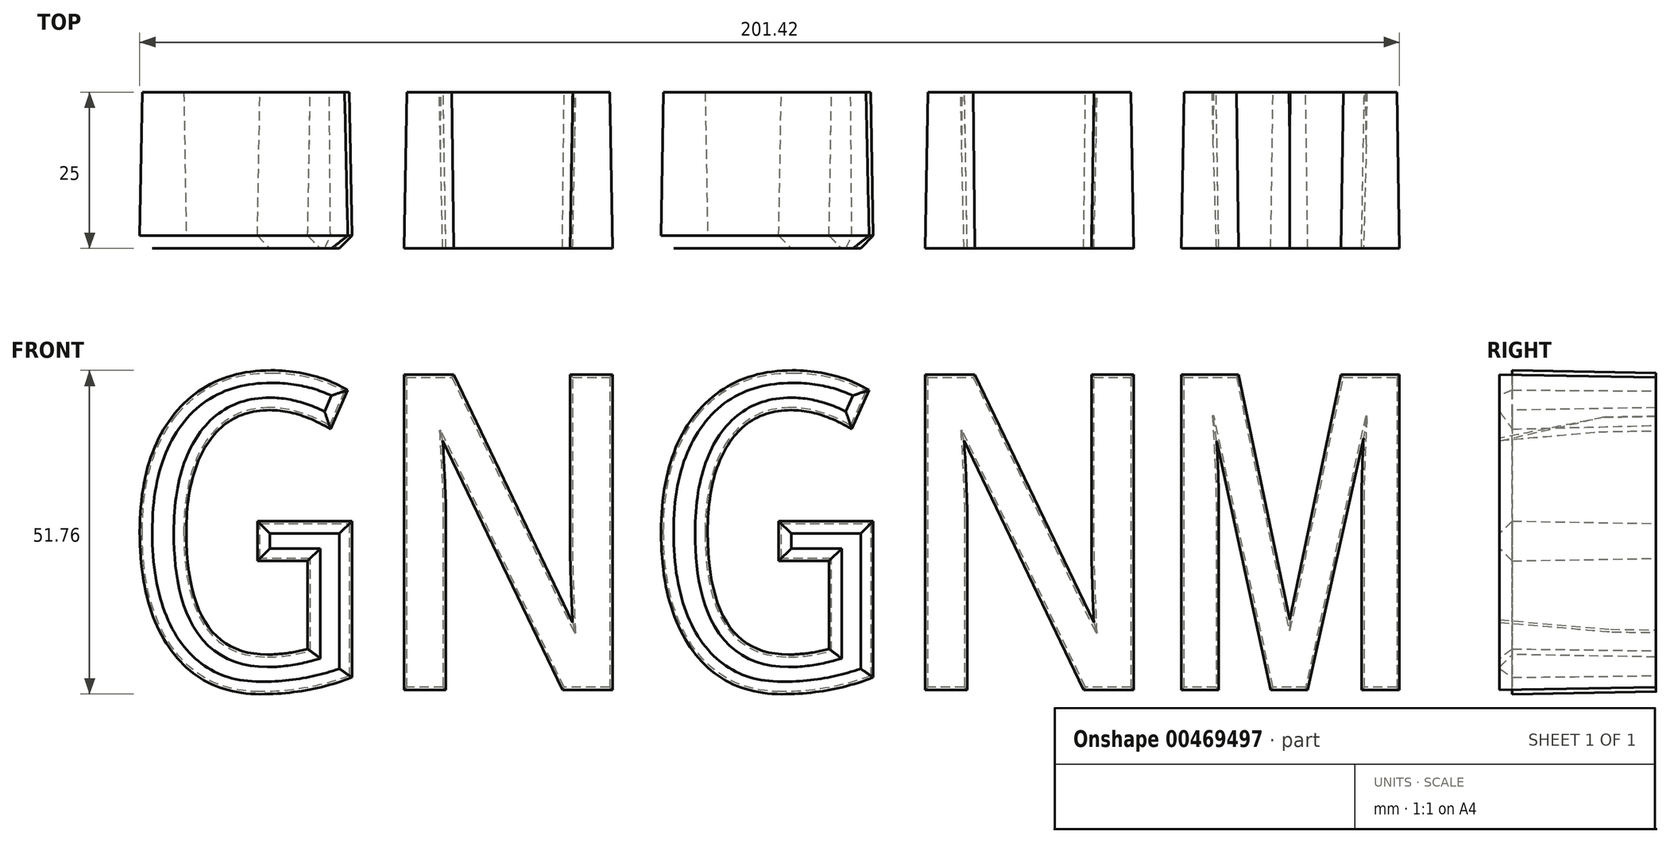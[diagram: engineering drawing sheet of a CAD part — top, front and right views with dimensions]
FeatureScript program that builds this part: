
annotation { "Feature Type Name" : "Feature", "Feature Type Description" : "" }
export const myFeature = defineFeature(function(context is Context, id is Id, definition is map)
    precondition{}
    {
        {
            var Q0;
            Q0=qCreatedBy(makeId("Front.planeOp"),FACE);
            var sketch = newSketch(context, id + "F0", { "sketchPlane" : qUnion([Q0])});
            skText(sketch, "E0", { "text": "GNGNM", "fontName": "DroidSansMono.ttf"});
            const initialGuessF0  = {"E0": [-0.03023, -0.02295, 1, 0, 0.05]};
            skSetInitialGuess(sketch, initialGuessF0);
            skSolve(sketch);
        }
        {
            var Q0;
            Q0=makeQuery(id+"F0.imprint","IMPRINT",FACE,{"disambiguationData":[TD([[makeQuery(id+"F0.imprint","IMPRINT",EDGE,{"derivedFrom":sQuery(id+"F0.wireOp",EDGE,"E0.sketch_text.stroke-17")}),-1.0]])]});
            var Q1;
            Q1=makeQuery(id+"F0.imprint","IMPRINT",FACE,{"disambiguationData":[TD([[makeQuery(id+"F0.imprint","IMPRINT",EDGE,{"derivedFrom":sQuery(id+"F0.wireOp",EDGE,"E0.sketch_text.stroke-0")}),-1.0]])]});
            var Q2;
            Q2=makeQuery(id+"F0.imprint","IMPRINT",FACE,{"disambiguationData":[TD([[makeQuery(id+"F0.imprint","IMPRINT",EDGE,{"derivedFrom":sQuery(id+"F0.wireOp",EDGE,"E0.sketch_text.stroke-31")}),-1.0]])]});
            var Q3;
            Q3=makeQuery(id+"F0.imprint","IMPRINT",FACE,{"disambiguationData":[TD([[makeQuery(id+"F0.imprint","IMPRINT",EDGE,{"derivedFrom":sQuery(id+"F0.wireOp",EDGE,"E0.sketch_text.stroke-48")}),-1.0]])]});
            var Q4;
            Q4=makeQuery(id+"F0.imprint","IMPRINT",FACE,{"disambiguationData":[TD([[makeQuery(id+"F0.imprint","IMPRINT",EDGE,{"derivedFrom":sQuery(id+"F0.wireOp",EDGE,"E0.sketch_text.stroke-62")}),-1.0]])]});
            extrude(context, id + "F1", {"entities" : qUnion([Q0, Q1, Q2, Q3, Q4]), "depth" : 25 * mm, "hasDraft" : true, "draftAngle" : 1 * degree});
        }
        {
            var Q0;
            Q0=makeQuery(id+"F1.opExtrude","CAP_EDGE",EDGE,{"disambiguationData":[OSD([sQuery(id+"F0.wireOp",EDGE,"E0.sketch_text.stroke-9")])],"isStart":false});
            var Q1;
            Q1=makeQuery(id+"F1.opExtrude","CAP_EDGE",EDGE,{"disambiguationData":[OSD([sQuery(id+"F0.wireOp",EDGE,"E0.sketch_text.stroke-10")])],"isStart":false});
            var Q2;
            Q2=makeQuery(id+"F1.opExtrude","CAP_EDGE",EDGE,{"disambiguationData":[OSD([sQuery(id+"F0.wireOp",EDGE,"E0.sketch_text.stroke-11")])],"isStart":false});
            var Q3;
            Q3=makeQuery(id+"F1.opExtrude","CAP_EDGE",EDGE,{"disambiguationData":[OSD([sQuery(id+"F0.wireOp",EDGE,"E0.sketch_text.stroke-12")])],"isStart":false});
            var Q4;
            Q4=makeQuery(id+"F1.opExtrude","CAP_EDGE",EDGE,{"disambiguationData":[OSD([sQuery(id+"F0.wireOp",EDGE,"E0.sketch_text.stroke-13")])],"isStart":false});
            var Q5;
            Q5=makeQuery(id+"F1.opExtrude","CAP_EDGE",EDGE,{"disambiguationData":[OSD([sQuery(id+"F0.wireOp",EDGE,"E0.sketch_text.stroke-14")])],"isStart":false});
            var Q6;
            Q6=makeQuery(id+"F1.opExtrude","CAP_EDGE",EDGE,{"disambiguationData":[OSD([sQuery(id+"F0.wireOp",EDGE,"E0.sketch_text.stroke-15")])],"isStart":false});
            var Q7;
            Q7=makeQuery(id+"F1.opExtrude","CAP_EDGE",EDGE,{"disambiguationData":[OSD([sQuery(id+"F0.wireOp",EDGE,"E0.sketch_text.stroke-16")])],"isStart":false});
            var Q8;
            Q8=makeQuery(id+"F1.opExtrude","CAP_EDGE",EDGE,{"disambiguationData":[OSD([sQuery(id+"F0.wireOp",EDGE,"E0.sketch_text.stroke-0")])],"isStart":false});
            var Q9;
            Q9=makeQuery(id+"F1.opExtrude","CAP_EDGE",EDGE,{"disambiguationData":[OSD([sQuery(id+"F0.wireOp",EDGE,"E0.sketch_text.stroke-1")])],"isStart":false});
            var Q10;
            Q10=makeQuery(id+"F1.opExtrude","CAP_EDGE",EDGE,{"disambiguationData":[OSD([sQuery(id+"F0.wireOp",EDGE,"E0.sketch_text.stroke-2")])],"isStart":false});
            var Q11;
            Q11=makeQuery(id+"F1.opExtrude","CAP_EDGE",EDGE,{"disambiguationData":[OSD([sQuery(id+"F0.wireOp",EDGE,"E0.sketch_text.stroke-3")])],"isStart":false});
            var Q12;
            Q12=makeQuery(id+"F1.opExtrude","CAP_EDGE",EDGE,{"disambiguationData":[OSD([sQuery(id+"F0.wireOp",EDGE,"E0.sketch_text.stroke-4")])],"isStart":false});
            var Q13;
            Q13=makeQuery(id+"F1.opExtrude","CAP_EDGE",EDGE,{"disambiguationData":[OSD([sQuery(id+"F0.wireOp",EDGE,"E0.sketch_text.stroke-5")])],"isStart":false});
            var Q14;
            Q14=makeQuery(id+"F1.opExtrude","CAP_EDGE",EDGE,{"disambiguationData":[OSD([sQuery(id+"F0.wireOp",EDGE,"E0.sketch_text.stroke-6")])],"isStart":false});
            var Q15;
            Q15=makeQuery(id+"F1.opExtrude","CAP_EDGE",EDGE,{"disambiguationData":[OSD([sQuery(id+"F0.wireOp",EDGE,"E0.sketch_text.stroke-7")])],"isStart":false});
            var Q16;
            Q16=makeQuery(id+"F1.opExtrude","CAP_EDGE",EDGE,{"disambiguationData":[OSD([sQuery(id+"F0.wireOp",EDGE,"E0.sketch_text.stroke-8")])],"isStart":false});
            var Q17;
            Q17=makeQuery(id+"F1.opExtrude","CAP_EDGE",EDGE,{"disambiguationData":[OSD([sQuery(id+"F0.wireOp",EDGE,"E0.sketch_text.stroke-23")])],"isStart":false});
            var Q18;
            Q18=makeQuery(id+"F1.opExtrude","CAP_EDGE",EDGE,{"disambiguationData":[OSD([sQuery(id+"F0.wireOp",EDGE,"E0.sketch_text.stroke-22")])],"isStart":false});
            var Q19;
            Q19=makeQuery(id+"F1.opExtrude","CAP_EDGE",EDGE,{"disambiguationData":[OSD([sQuery(id+"F0.wireOp",EDGE,"E0.sketch_text.stroke-21")])],"isStart":false});
            var Q20;
            Q20=makeQuery(id+"F1.opExtrude","CAP_EDGE",EDGE,{"disambiguationData":[OSD([sQuery(id+"F0.wireOp",EDGE,"E0.sketch_text.stroke-20")])],"isStart":false});
            var Q21;
            Q21=makeQuery(id+"F1.opExtrude","CAP_EDGE",EDGE,{"disambiguationData":[OSD([sQuery(id+"F0.wireOp",EDGE,"E0.sketch_text.stroke-18")])],"isStart":false});
            var Q22;
            Q22=makeQuery(id+"F1.opExtrude","CAP_EDGE",EDGE,{"disambiguationData":[OSD([sQuery(id+"F0.wireOp",EDGE,"E0.sketch_text.stroke-24")])],"isStart":false});
            var Q23;
            Q23=makeQuery(id+"F1.opExtrude","CAP_EDGE",EDGE,{"disambiguationData":[OSD([sQuery(id+"F0.wireOp",EDGE,"E0.sketch_text.stroke-25")])],"isStart":false});
            var Q24;
            Q24=makeQuery(id+"F1.opExtrude","CAP_EDGE",EDGE,{"disambiguationData":[OSD([sQuery(id+"F0.wireOp",EDGE,"E0.sketch_text.stroke-28")])],"isStart":false});
            var Q25;
            Q25=makeQuery(id+"F1.opExtrude","CAP_EDGE",EDGE,{"disambiguationData":[OSD([sQuery(id+"F0.wireOp",EDGE,"E0.sketch_text.stroke-29")])],"isStart":false});
            var Q26;
            Q26=makeQuery(id+"F1.opExtrude","CAP_EDGE",EDGE,{"disambiguationData":[OSD([sQuery(id+"F0.wireOp",EDGE,"E0.sketch_text.stroke-30")])],"isStart":false});
            var Q27;
            Q27=makeQuery(id+"F1.opExtrude","CAP_EDGE",EDGE,{"disambiguationData":[OSD([sQuery(id+"F0.wireOp",EDGE,"E0.sketch_text.stroke-17")])],"isStart":false});
            var Q28;
            Q28=makeQuery(id+"F1.opExtrude","CAP_EDGE",EDGE,{"disambiguationData":[OSD([sQuery(id+"F0.wireOp",EDGE,"E0.sketch_text.stroke-33")])],"isStart":false});
            var Q29;
            Q29=makeQuery(id+"F1.opExtrude","CAP_EDGE",EDGE,{"disambiguationData":[OSD([sQuery(id+"F0.wireOp",EDGE,"E0.sketch_text.stroke-34")])],"isStart":false});
            var Q30;
            Q30=makeQuery(id+"F1.opExtrude","CAP_EDGE",EDGE,{"disambiguationData":[OSD([sQuery(id+"F0.wireOp",EDGE,"E0.sketch_text.stroke-35")])],"isStart":false});
            var Q31;
            Q31=makeQuery(id+"F1.opExtrude","CAP_EDGE",EDGE,{"disambiguationData":[OSD([sQuery(id+"F0.wireOp",EDGE,"E0.sketch_text.stroke-36")])],"isStart":false});
            var Q32;
            Q32=makeQuery(id+"F1.opExtrude","CAP_EDGE",EDGE,{"disambiguationData":[OSD([sQuery(id+"F0.wireOp",EDGE,"E0.sketch_text.stroke-37")])],"isStart":false});
            var Q33;
            Q33=makeQuery(id+"F1.opExtrude","CAP_EDGE",EDGE,{"disambiguationData":[OSD([sQuery(id+"F0.wireOp",EDGE,"E0.sketch_text.stroke-38")])],"isStart":false});
            var Q34;
            Q34=makeQuery(id+"F1.opExtrude","CAP_EDGE",EDGE,{"disambiguationData":[OSD([sQuery(id+"F0.wireOp",EDGE,"E0.sketch_text.stroke-39")])],"isStart":false});
            var Q35;
            Q35=makeQuery(id+"F1.opExtrude","CAP_EDGE",EDGE,{"disambiguationData":[OSD([sQuery(id+"F0.wireOp",EDGE,"E0.sketch_text.stroke-40")])],"isStart":false});
            var Q36;
            Q36=makeQuery(id+"F1.opExtrude","CAP_EDGE",EDGE,{"disambiguationData":[OSD([sQuery(id+"F0.wireOp",EDGE,"E0.sketch_text.stroke-42")])],"isStart":false});
            var Q37;
            Q37=makeQuery(id+"F1.opExtrude","CAP_EDGE",EDGE,{"disambiguationData":[OSD([sQuery(id+"F0.wireOp",EDGE,"E0.sketch_text.stroke-41")])],"isStart":false});
            var Q38;
            Q38=makeQuery(id+"F1.opExtrude","CAP_EDGE",EDGE,{"disambiguationData":[OSD([sQuery(id+"F0.wireOp",EDGE,"E0.sketch_text.stroke-43")])],"isStart":false});
            var Q39;
            Q39=makeQuery(id+"F1.opExtrude","CAP_EDGE",EDGE,{"disambiguationData":[OSD([sQuery(id+"F0.wireOp",EDGE,"E0.sketch_text.stroke-44")])],"isStart":false});
            var Q40;
            Q40=makeQuery(id+"F1.opExtrude","CAP_EDGE",EDGE,{"disambiguationData":[OSD([sQuery(id+"F0.wireOp",EDGE,"E0.sketch_text.stroke-45")])],"isStart":false});
            var Q41;
            Q41=makeQuery(id+"F1.opExtrude","CAP_EDGE",EDGE,{"disambiguationData":[OSD([sQuery(id+"F0.wireOp",EDGE,"E0.sketch_text.stroke-46")])],"isStart":false});
            var Q42;
            Q42=makeQuery(id+"F1.opExtrude","CAP_EDGE",EDGE,{"disambiguationData":[OSD([sQuery(id+"F0.wireOp",EDGE,"E0.sketch_text.stroke-47")])],"isStart":false});
            var Q43;
            Q43=makeQuery(id+"F1.opExtrude","CAP_EDGE",EDGE,{"disambiguationData":[OSD([sQuery(id+"F0.wireOp",EDGE,"E0.sketch_text.stroke-31")])],"isStart":false});
            var Q44;
            Q44=makeQuery(id+"F1.opExtrude","CAP_EDGE",EDGE,{"disambiguationData":[OSD([sQuery(id+"F0.wireOp",EDGE,"E0.sketch_text.stroke-32")])],"isStart":false});
            var Q45;
            Q45=makeQuery(id+"F1.opExtrude","CAP_EDGE",EDGE,{"disambiguationData":[OSD([sQuery(id+"F0.wireOp",EDGE,"E0.sketch_text.stroke-53")])],"isStart":false});
            var Q46;
            Q46=makeQuery(id+"F1.opExtrude","CAP_EDGE",EDGE,{"disambiguationData":[OSD([sQuery(id+"F0.wireOp",EDGE,"E0.sketch_text.stroke-54")])],"isStart":false});
            var Q47;
            Q47=makeQuery(id+"F1.opExtrude","CAP_EDGE",EDGE,{"disambiguationData":[OSD([sQuery(id+"F0.wireOp",EDGE,"E0.sketch_text.stroke-52")])],"isStart":false});
            var Q48;
            Q48=makeQuery(id+"F1.opExtrude","CAP_EDGE",EDGE,{"disambiguationData":[OSD([sQuery(id+"F0.wireOp",EDGE,"E0.sketch_text.stroke-51")])],"isStart":false});
            var Q49;
            Q49=makeQuery(id+"F1.opExtrude","CAP_EDGE",EDGE,{"disambiguationData":[OSD([sQuery(id+"F0.wireOp",EDGE,"E0.sketch_text.stroke-49")])],"isStart":false});
            var Q50;
            Q50=makeQuery(id+"F1.opExtrude","CAP_EDGE",EDGE,{"disambiguationData":[OSD([sQuery(id+"F0.wireOp",EDGE,"E0.sketch_text.stroke-56")])],"isStart":false});
            var Q51;
            Q51=makeQuery(id+"F1.opExtrude","CAP_EDGE",EDGE,{"disambiguationData":[OSD([sQuery(id+"F0.wireOp",EDGE,"E0.sketch_text.stroke-55")])],"isStart":false});
            var Q52;
            Q52=makeQuery(id+"F1.opExtrude","CAP_EDGE",EDGE,{"disambiguationData":[OSD([sQuery(id+"F0.wireOp",EDGE,"E0.sketch_text.stroke-48")])],"isStart":false});
            var Q53;
            Q53=makeQuery(id+"F1.opExtrude","CAP_EDGE",EDGE,{"disambiguationData":[OSD([sQuery(id+"F0.wireOp",EDGE,"E0.sketch_text.stroke-61")])],"isStart":false});
            var Q54;
            Q54=makeQuery(id+"F1.opExtrude","CAP_EDGE",EDGE,{"disambiguationData":[OSD([sQuery(id+"F0.wireOp",EDGE,"E0.sketch_text.stroke-59")])],"isStart":false});
            var Q55;
            Q55=makeQuery(id+"F1.opExtrude","CAP_EDGE",EDGE,{"disambiguationData":[OSD([sQuery(id+"F0.wireOp",EDGE,"E0.sketch_text.stroke-58")])],"isStart":false});
            var Q56;
            Q56=makeQuery(id+"F1.opExtrude","CAP_EDGE",EDGE,{"disambiguationData":[OSD([sQuery(id+"F0.wireOp",EDGE,"E0.sketch_text.stroke-60")])],"isStart":false});
            var Q57;
            Q57=makeQuery(id+"F1.opExtrude","CAP_EDGE",EDGE,{"disambiguationData":[OSD([sQuery(id+"F0.wireOp",EDGE,"E0.sketch_text.stroke-67")])],"isStart":false});
            var Q58;
            Q58=makeQuery(id+"F1.opExtrude","CAP_EDGE",EDGE,{"disambiguationData":[OSD([sQuery(id+"F0.wireOp",EDGE,"E0.sketch_text.stroke-66")])],"isStart":false});
            var Q59;
            Q59=makeQuery(id+"F1.opExtrude","CAP_EDGE",EDGE,{"disambiguationData":[OSD([sQuery(id+"F0.wireOp",EDGE,"E0.sketch_text.stroke-65")])],"isStart":false});
            var Q60;
            Q60=makeQuery(id+"F1.opExtrude","CAP_EDGE",EDGE,{"disambiguationData":[OSD([sQuery(id+"F0.wireOp",EDGE,"E0.sketch_text.stroke-68")])],"isStart":false});
            var Q61;
            Q61=makeQuery(id+"F1.opExtrude","CAP_EDGE",EDGE,{"disambiguationData":[OSD([sQuery(id+"F0.wireOp",EDGE,"E0.sketch_text.stroke-64")])],"isStart":false});
            var Q62;
            Q62=makeQuery(id+"F1.opExtrude","CAP_EDGE",EDGE,{"disambiguationData":[OSD([sQuery(id+"F0.wireOp",EDGE,"E0.sketch_text.stroke-62")])],"isStart":false});
            var Q63;
            Q63=makeQuery(id+"F1.opExtrude","CAP_EDGE",EDGE,{"disambiguationData":[OSD([sQuery(id+"F0.wireOp",EDGE,"E0.sketch_text.stroke-79")])],"isStart":false});
            var Q64;
            Q64=makeQuery(id+"F1.opExtrude","CAP_EDGE",EDGE,{"disambiguationData":[OSD([sQuery(id+"F0.wireOp",EDGE,"E0.sketch_text.stroke-78")])],"isStart":false});
            var Q65;
            Q65=makeQuery(id+"F1.opExtrude","CAP_EDGE",EDGE,{"disambiguationData":[OSD([sQuery(id+"F0.wireOp",EDGE,"E0.sketch_text.stroke-69")])],"isStart":false});
            var Q66;
            Q66=makeQuery(id+"F1.opExtrude","CAP_EDGE",EDGE,{"disambiguationData":[OSD([sQuery(id+"F0.wireOp",EDGE,"E0.sketch_text.stroke-71")])],"isStart":false});
            var Q67;
            Q67=makeQuery(id+"F1.opExtrude","CAP_EDGE",EDGE,{"disambiguationData":[OSD([sQuery(id+"F0.wireOp",EDGE,"E0.sketch_text.stroke-75")])],"isStart":false});
            var Q68;
            Q68=makeQuery(id+"F1.opExtrude","CAP_EDGE",EDGE,{"disambiguationData":[OSD([sQuery(id+"F0.wireOp",EDGE,"E0.sketch_text.stroke-73")])],"isStart":false});
            var Q69;
            Q69=makeQuery(id+"F1.opExtrude","CAP_EDGE",EDGE,{"disambiguationData":[OSD([sQuery(id+"F0.wireOp",EDGE,"E0.sketch_text.stroke-76")])],"isStart":false});
            var Q70;
            Q70=makeQuery(id+"F1.opExtrude","CAP_EDGE",EDGE,{"disambiguationData":[OSD([sQuery(id+"F0.wireOp",EDGE,"E0.sketch_text.stroke-74")])],"isStart":false});
            var Q71;
            Q71=makeQuery(id+"F1.opExtrude","CAP_EDGE",EDGE,{"disambiguationData":[OSD([sQuery(id+"F0.wireOp",EDGE,"E0.sketch_text.stroke-72")])],"isStart":false});
            chamfer(context, id + "F2", {"entities" : qUnion([Q0, Q1, Q2, Q3, Q4, Q5, Q6, Q7, Q8, Q9, Q10, Q11, Q12, Q13, Q14, Q15, Q16, Q17, Q18, Q19, Q20, Q21, Q22, Q23, Q24, Q25, Q26, Q27, Q28, Q29, Q30, Q31, Q32, Q33, Q34, Q35, Q36, Q37, Q38, Q39, Q40, Q41, Q42, Q43, Q44, Q45, Q46, Q47, Q48, Q49, Q50, Q51, Q52, Q53, Q54, Q55, Q56, Q57, Q58, Q59, Q60, Q61, Q62, Q63, Q64, Q65, Q66, Q67, Q68, Q69, Q70, Q71]), "width" : 2 * mm, "tangentPropagation" : true});
        }
    });
